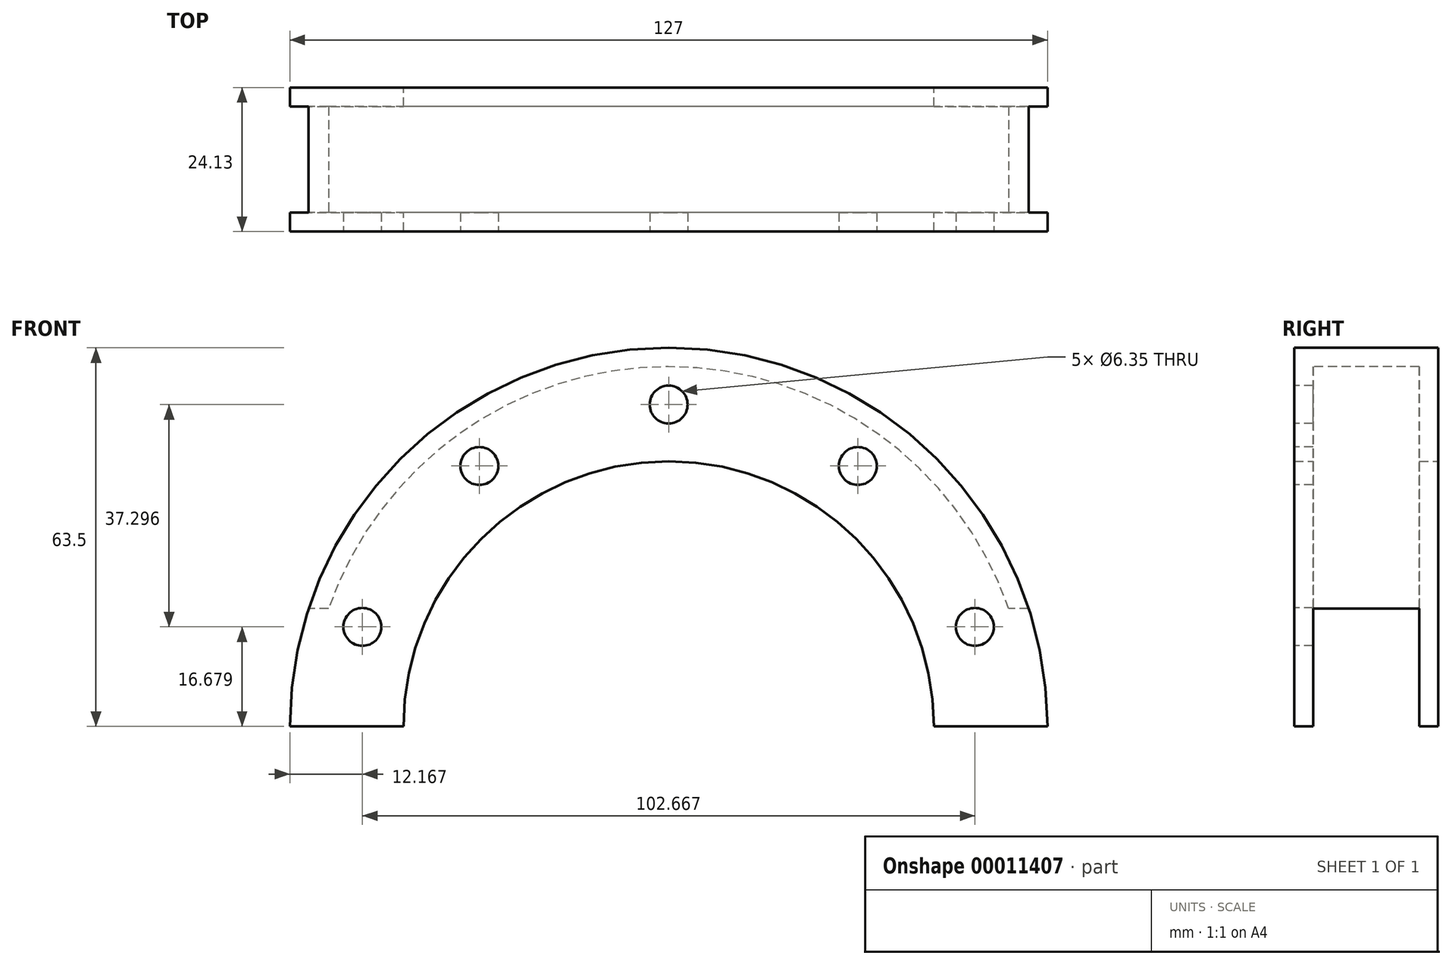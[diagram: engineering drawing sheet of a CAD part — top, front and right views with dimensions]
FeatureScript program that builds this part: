
annotation { "Feature Type Name" : "Feature", "Feature Type Description" : "" }
export const myFeature = defineFeature(function(context is Context, id is Id, definition is map)
    precondition{}
    {
        {
            var Q0;
            Q0=qCreatedBy(makeId("Front.planeOp"),FACE);
            var sketch = newSketch(context, id + "F0", { "sketchPlane" : qUnion([Q0])});
            skArc(sketch, "E0", {"start": v(44.45, 0) * mm, "mid": v(0, 44.45) * mm, "end": v(-44.45, 0) * mm});
            skArc(sketch, "E1", {"start": v(63.5, 0) * mm, "mid": v(0, 63.5) * mm, "end": v(-63.5, 0) * mm});
            skPoint(sketch, "E2.end.orphan", {"position": v(-63.5, 0) * mm});
            skPoint(sketch, "E3.orphan", {"position": v(63.5, 0) * mm});
            skLineSegment(sketch, "E4", {"start": v(-63.5, 0) * mm, "end": v(-44.45, 0) * mm});
            skLineSegment(sketch, "E5", {"start": v(44.45, 0) * mm, "end": v(63.5, 0) * mm});
            skSolve(sketch);
        }
        {
            var Q0;
            Q0 = qSketchRegion(id + "F0", true);
            extrude(context, id + "F1", {"entities" : qUnion([Q0]), "endBound" : BoundingType.SYMMETRIC, "depth" : 24.13 * mm});
        }
        {
            var Q0;
            Q0=qCreatedBy(makeId("Front.planeOp"),FACE);
            var sketch = newSketch(context, id + "F2", { "sketchPlane" : qUnion([Q0])});
            skArc(sketch, "E6", {"start": v(57, 19.74) * mm, "mid": v(0, 60.32) * mm, "end": v(-57, 19.73) * mm});
            skLineSegment(sketch, "E7", {"start": v(-57, 19.73) * mm, "end": v(-93.45, 19.73) * mm});
            skLineSegment(sketch, "E8", {"start": v(-93.45, 19.73) * mm, "end": v(-94.38, -23.44) * mm});
            skLineSegment(sketch, "E9", {"start": v(-94.38, -23.44) * mm, "end": v(83.48, -23.44) * mm});
            skLineSegment(sketch, "E10", {"start": v(83.48, -23.44) * mm, "end": v(83.48, 19.74) * mm});
            skLineSegment(sketch, "E11", {"start": v(83.48, 19.74) * mm, "end": v(57, 19.74) * mm});
            skSolve(sketch);
        }
        {
            var Q0;
            Q0 = qSketchRegion(id + "F2", true);
            extrude(context, id + "F3", {"entities" : qUnion([Q0]), "operationType" : NewBodyOperationType.REMOVE, "endBound" : BoundingType.SYMMETRIC, "oppositeDirection" : true, "depth" : 17.78 * mm});
        }
        {
            var Q0;
            Q0=makeQuery(id+"F1.opExtrude","CAP_FACE",FACE,{"disambiguationData":[OSD([sQuery(id+"F0.wireOp",EDGE,"E0"),sQuery(id+"F0.wireOp",EDGE,"E1"),sQuery(id+"F0.wireOp",EDGE,"97f9939d-f5dc-4f5a-8dc0-db47485ad3c5"),sQuery(id+"F0.wireOp",EDGE,"7ff83e86-972c-44cd-90d0-3de2b4139a94"),sQuery(id+"F0.wireOp",EDGE,"543a905b-a2b6-43e6-bd61-41bc61abd503"),sQuery(id+"F0.wireOp",EDGE,"60758327-1bac-4290-bd68-b8ccbb937547"),sQuery(id+"F0.wireOp",EDGE,"1918a5e7-a803-4cd7-b953-43989ceaabd4"),sQuery(id+"F0.wireOp",EDGE,"3fec647a-ee68-4e55-bca9-01a08b1f4607"),sQuery(id+"F0.wireOp",EDGE,"ab8a5607-ba6f-4a88-9e8e-3d86bb481dd7"),sQuery(id+"F0.wireOp",EDGE,"c15b8bb0-3f1b-4a56-bdc3-407ecf3bdc5c"),sQuery(id+"F0.wireOp",EDGE,"227e1d02-05bb-4da7-be26-47de3a556081"),sQuery(id+"F0.wireOp",EDGE,"a3d37f6d-04d1-4360-a315-4a20df1ecd6f"),sQuery(id+"F0.wireOp",EDGE,"237d7851-e342-4e87-93a3-89f51ee1ed5b"),sQuery(id+"F0.wireOp",EDGE,"8101a5a3-5c74-4245-9cd7-3f7285bb0dae")])],"isStart":false});
            var sketch = newSketch(context, id + "F4", { "sketchPlane" : qUnion([Q0])});
            skCircle(sketch, "E12", {"center": v(0, 0) * mm, "radius": 53.98 * mm, "construction": true});
            skCircle(sketch, "E13", {"center": v(0, 53.98) * mm, "radius": 3.18 * mm});
            skCircle(sketch, "E14.1.0", {"center": v(-31.73, 43.67) * mm, "radius": 3.18 * mm});
            skCircle(sketch, "E14.2.0", {"center": v(-51.33, 16.68) * mm, "radius": 3.18 * mm});
            skCircle(sketch, "E14.3.0", {"center": v(-51.33, -16.68) * mm, "radius": 3.18 * mm});
            skCircle(sketch, "E14.4.0", {"center": v(-31.73, -43.67) * mm, "radius": 3.18 * mm});
            skCircle(sketch, "E14.5.0", {"center": v(0, -53.98) * mm, "radius": 3.18 * mm});
            skCircle(sketch, "E14.6.0", {"center": v(31.73, -43.67) * mm, "radius": 3.18 * mm});
            skCircle(sketch, "E14.7.0", {"center": v(51.33, -16.68) * mm, "radius": 3.18 * mm});
            skCircle(sketch, "E14.8.0", {"center": v(51.33, 16.68) * mm, "radius": 3.18 * mm});
            skCircle(sketch, "E14.9.0", {"center": v(31.73, 43.67) * mm, "radius": 3.18 * mm});
            skSolve(sketch);
        }
        {
            var Q0;
            Q0 = qSketchRegion(id + "F4", true);
            extrude(context, id + "F5", {"entities" : qUnion([Q0]), "operationType" : NewBodyOperationType.REMOVE, "oppositeDirection" : true, "depth" : 7.62 * mm});
        }
    });
